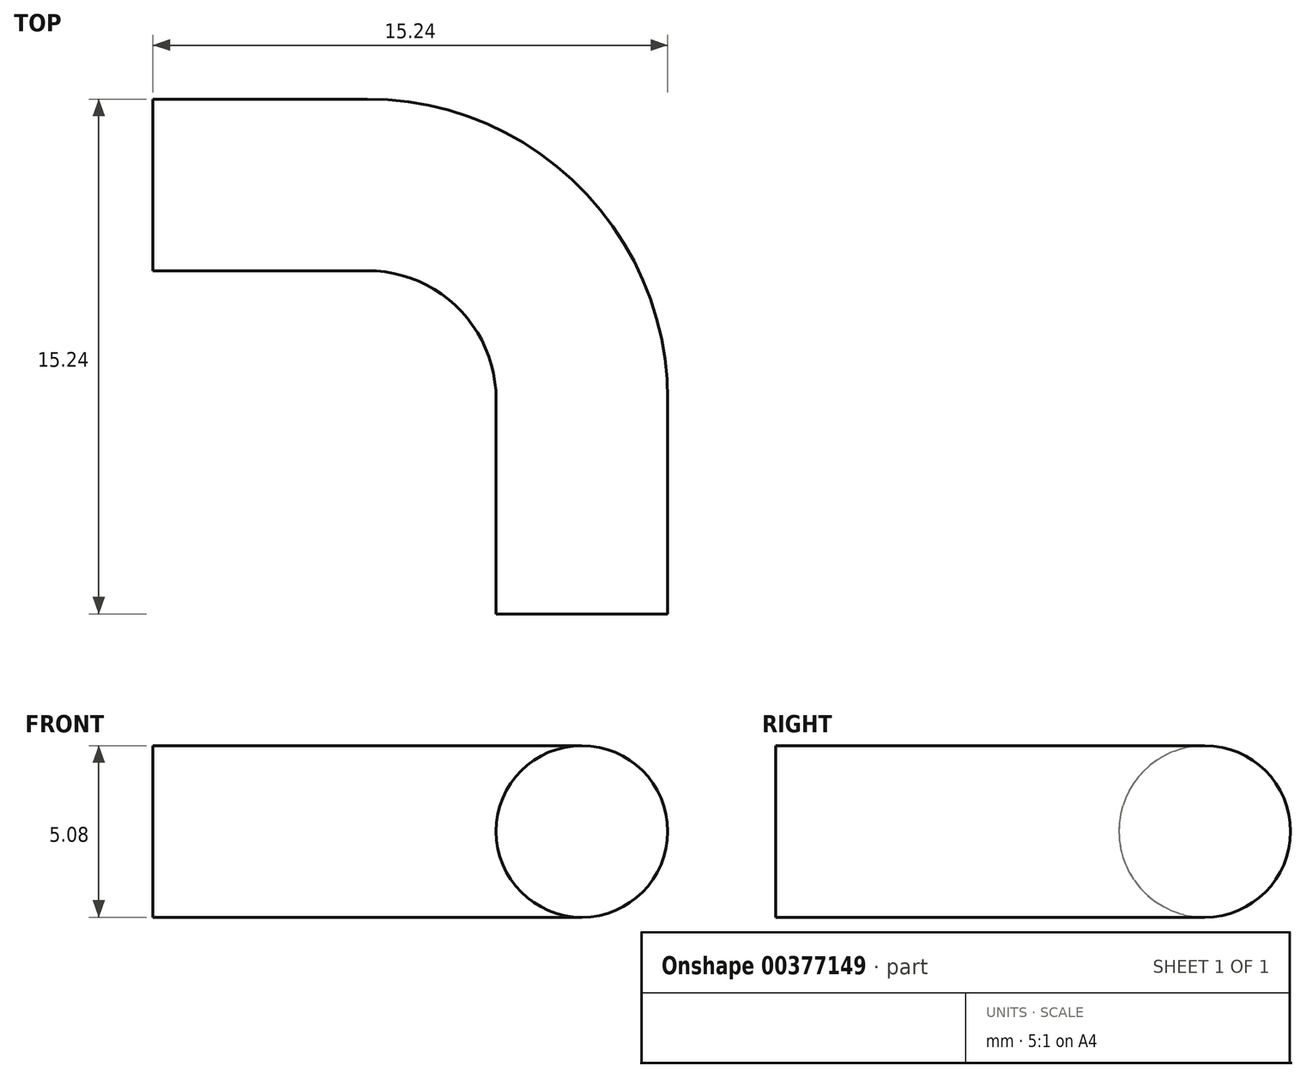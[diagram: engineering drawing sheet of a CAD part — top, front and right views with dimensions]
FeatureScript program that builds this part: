
annotation { "Feature Type Name" : "Feature", "Feature Type Description" : "" }
export const myFeature = defineFeature(function(context is Context, id is Id, definition is map)
    precondition{}
    {
        {
            var Q0;
            Q0=qCreatedBy(makeId("Top.planeOp"),FACE);
            var sketch = newSketch(context, id + "F0", { "sketchPlane" : qUnion([Q0])});
            skLineSegment(sketch, "E0", {"start": v(0, 0) * mm, "end": v(0, 6.35) * mm});
            skLineSegment(sketch, "E1", {"start": v(-6.35, 12.7) * mm, "end": v(-12.7, 12.7) * mm});
            skPoint(sketch, "E2.visualSharp", {"position": v(0, 12.7) * mm});
            skArc(sketch, "E2.filletArc", {"start": v(0, 6.35) * mm, "mid": v(-1.86, 10.84) * mm, "end": v(-6.35, 12.7) * mm});
            skLineSegment(sketch, "E3", {"start": v(0, 0) * mm, "end": v(0, -127) * mm});
            skSolve(sketch);
        }
        {
            var Q0;
            Q0=qCreatedBy(makeId("Front.planeOp"),FACE);
            var sketch = newSketch(context, id + "F1", { "sketchPlane" : qUnion([Q0])});
            skCircle(sketch, "E4", {"center": v(0, 0) * mm, "radius": 2.54 * mm});
            skCircle(sketch, "E5", {"center": v(0, 0) * mm, "radius": 6.35 * mm});
            skSolve(sketch);
        }
        {
            var Q0;
            Q0=makeQuery(id+"F1.imprint","IMPRINT",FACE,{"disambiguationData":[TD([[makeQuery(id+"F1.imprint","IMPRINT",EDGE,{"derivedFrom":sQuery(id+"F1.wireOp",EDGE,"E4")}),1.0]])]});
            var Q1;
            Q1=sQuery(id+"F0.wireOp",EDGE,"E1");
            var Q2;
            Q2=sQuery(id+"F0.wireOp",EDGE,"E2.filletArc");
            var Q3;
            Q3=sQuery(id+"F0.wireOp",EDGE,"E0");
            sweep(context, id + "F2", {"profiles" : qUnion([Q0]), "path" : qUnion([Q1, Q2, Q3])});
        }
    });
